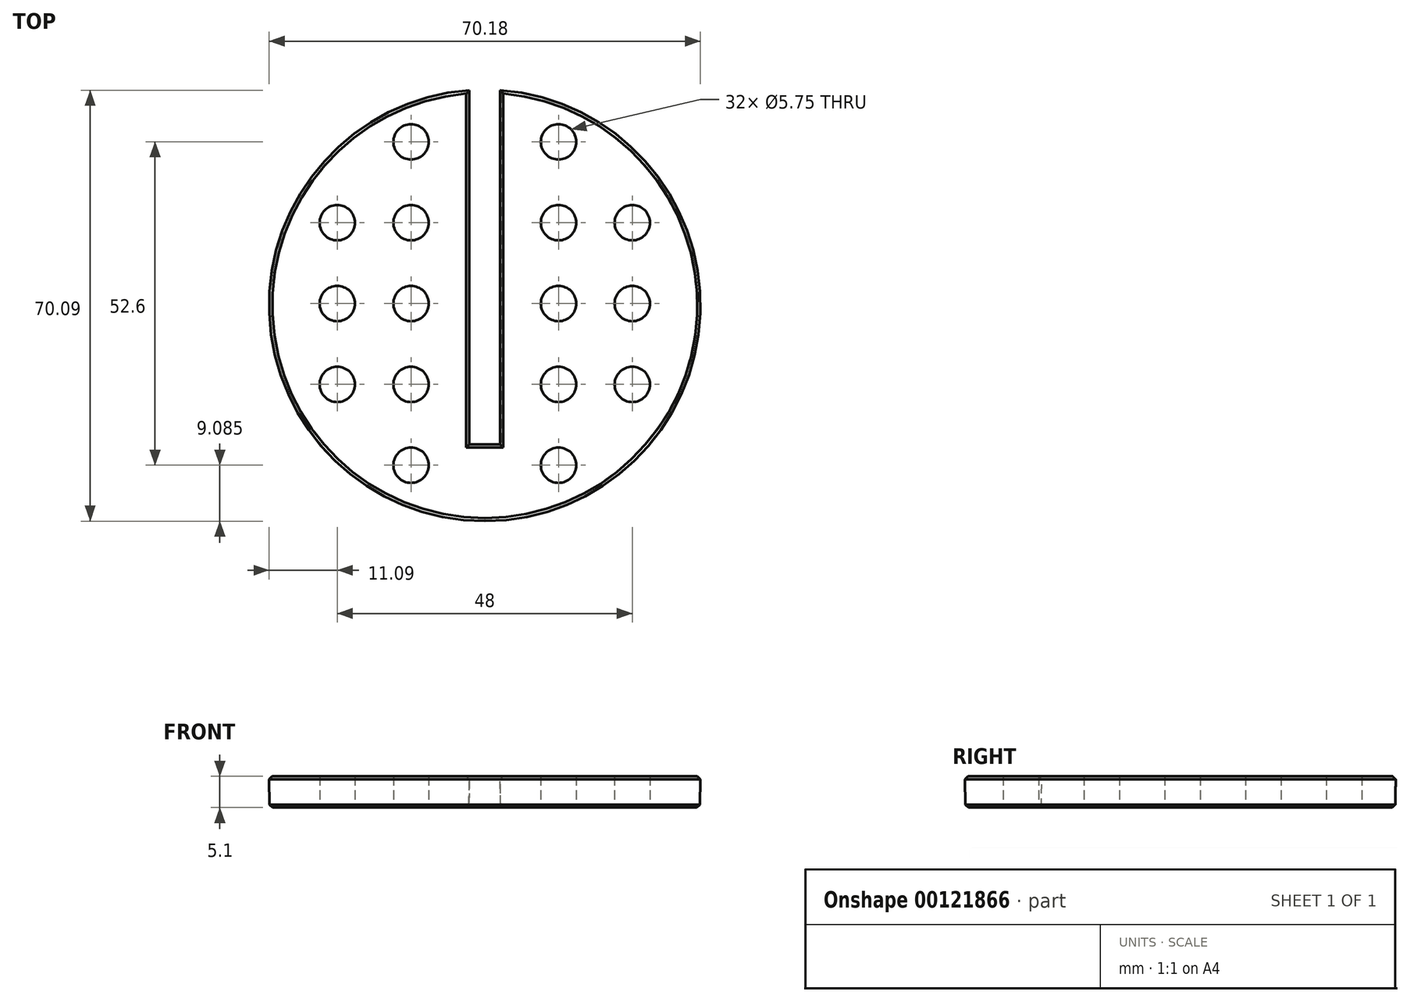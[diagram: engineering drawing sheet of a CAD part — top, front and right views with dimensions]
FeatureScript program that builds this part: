
annotation { "Feature Type Name" : "Feature", "Feature Type Description" : "" }
export const myFeature = defineFeature(function(context is Context, id is Id, definition is map)
    precondition{}
    {
        {
            var Q0;
            Q0=qCreatedBy(makeId("Top.planeOp"),FACE);
            var sketch = newSketch(context, id + "F0", { "sketchPlane" : qUnion([Q0])});
            skCircle(sketch, "E0", {"center": v(0, 0) * mm, "radius": 35.1 * mm});
            skPoint(sketch, "E1", {"position": v(-2.5, 0) * mm});
            skPoint(sketch, "E2", {"position": v(2.5, 0) * mm});
            skPoint(sketch, "E3", {"position": v(0, -35.1) * mm});
            skPoint(sketch, "E4", {"position": v(0, -22.6) * mm});
            skLineSegment(sketch, "E5", {"start": v(-2.5, 35) * mm, "end": v(-2.5, -22.6) * mm});
            skLineSegment(sketch, "E6", {"start": v(2.5, 35) * mm, "end": v(2.5, -22.6) * mm});
            skLineSegment(sketch, "E7", {"start": v(2.5, -22.6) * mm, "end": v(-2.5, -22.6) * mm});
            skPoint(sketch, "E8", {"position": v(-12, 26.6) * mm});
            skPoint(sketch, "E9.0.1.0", {"position": v(-12, 13.44) * mm});
            skPoint(sketch, "E9.0.2.0", {"position": v(-12, 0.3) * mm});
            skPoint(sketch, "E9.0.3.0", {"position": v(-12, -12.86) * mm});
            skPoint(sketch, "E9.0.4.0", {"position": v(-12, -26) * mm});
            skPoint(sketch, "E9.1.0.0", {"position": v(-24, 26.6) * mm});
            skPoint(sketch, "E9.1.1.0", {"position": v(-24, 13.44) * mm});
            skPoint(sketch, "E9.1.2.0", {"position": v(-24, 0.3) * mm});
            skPoint(sketch, "E9.1.3.0", {"position": v(-24, -12.86) * mm});
            skPoint(sketch, "E9.1.4.0", {"position": v(-24, -26) * mm});
            skLineSegment(sketch, "E9.direction1", {"start": v(-12, 26.6) * mm, "end": v(-24, 26.6) * mm, "construction": true});
            skLineSegment(sketch, "E9.direction2", {"start": v(-12, 26.6) * mm, "end": v(-12, 13.44) * mm, "construction": true});
            skPoint(sketch, "E10", {"position": v(0, 35.1) * mm});
            skLineSegment(sketch, "E11", {"start": v(0, 43.08) * mm, "end": v(0, -42.45) * mm, "construction": true});
            skPoint(sketch, "E12.MirrorP", {"position": v(24, -12.85) * mm});
            skPoint(sketch, "E13.MirrorP", {"position": v(24, 0.3) * mm});
            skPoint(sketch, "E14.MirrorP", {"position": v(24, 13.45) * mm});
            skPoint(sketch, "E15.MirrorP", {"position": v(12, -26) * mm});
            skPoint(sketch, "E16.MirrorP", {"position": v(12, -12.85) * mm});
            skPoint(sketch, "E17.MirrorP", {"position": v(12, 0.3) * mm});
            skPoint(sketch, "E18.MirrorP", {"position": v(12, 13.45) * mm});
            skPoint(sketch, "E19.MirrorP", {"position": v(12, 26.6) * mm});
            skSolve(sketch);
        }
        {
            var Q0;
            {var subQ0=sQuery(id+"F0.wireOp",EDGE,"E5");Q0=makeQuery(id+"F0.imprint","IMPRINT",FACE,{"disambiguationData":[TD([[makeQuery(id+"F0.imprint","IMPRINT",EDGE,{"derivedFrom":subQ0}),-1.0]])]});}
            extrude(context, id + "F1", {"entities" : qUnion([Q0]), "oppositeDirection" : true, "depth" : (4.72 + .381) * mm, "hasDraft" : true, "draftAngle" : 1 * degree, "draftPullDirection" : true});
        }
        {
            var Q0;
            Q0=sQuery(id+"F0.wireOp",VERTEX,"E8");
            var Q1;
            Q1=sQuery(id+"F0.wireOp",VERTEX,"E9.0.1.0");
            var Q2;
            Q2=sQuery(id+"F0.wireOp",VERTEX,"E9.0.2.0");
            var Q3;
            Q3=sQuery(id+"F0.wireOp",VERTEX,"E9.0.3.0");
            var Q4;
            Q4=sQuery(id+"F0.wireOp",VERTEX,"E9.1.2.0");
            var Q5;
            Q5=sQuery(id+"F0.wireOp",VERTEX,"E9.1.3.0");
            var Q6;
            Q6=sQuery(id+"F0.wireOp",VERTEX,"E9.1.1.0");
            var Q7;
            Q7=sQuery(id+"F0.wireOp",VERTEX,"E9.0.4.0");
            var Q8;
            Q8=sQuery(id+"F0.wireOp",VERTEX,"E14.MirrorP");
            var Q9;
            Q9=sQuery(id+"F0.wireOp",VERTEX,"E19.MirrorP");
            var Q10;
            Q10=sQuery(id+"F0.wireOp",VERTEX,"E15.MirrorP");
            var Q11;
            Q11=sQuery(id+"F0.wireOp",VERTEX,"E17.MirrorP");
            var Q12;
            Q12=sQuery(id+"F0.wireOp",VERTEX,"E12.MirrorP");
            var Q13;
            Q13=sQuery(id+"F0.wireOp",VERTEX,"E13.MirrorP");
            var Q14;
            Q14=sQuery(id+"F0.wireOp",VERTEX,"E18.MirrorP");
            var Q15;
            Q15=sQuery(id+"F0.wireOp",VERTEX,"E16.MirrorP");
            var Q16;
            Q16=makeQuery(id+"F1.opExtrude","SWEPT_BODY",BODY,{"disambiguationData":[OSD([sQuery(id+"F0.wireOp",EDGE,"E0"),sQuery(id+"F0.wireOp",EDGE,"E5"),sQuery(id+"F0.wireOp",EDGE,"E6"),sQuery(id+"F0.wireOp",EDGE,"E7")])]});
            hole(context, id + "F2", {"style" : HoleStyle.SIMPLE, "endStyle" : HoleEndStyle.BLIND, "holeDiameter" : 5.75 * mm, "holeDepth" : 7 * mm, "locations" : qUnion([Q0, Q1, Q2, Q3, Q4, Q5, Q6, Q7, Q8, Q9, Q10, Q11, Q12, Q13, Q14, Q15]), "scope" : qUnion([Q16])});
        }
        {
            var Q0;
            Q0=makeQuery(id+"F1.opExtrude","CAP_EDGE",EDGE,{"disambiguationData":[OSD([sQuery(id+"F0.wireOp",EDGE,"E0")])],"isStart":true});
            var Q1;
            Q1=makeQuery(id+"F1.opExtrude","CAP_EDGE",EDGE,{"disambiguationData":[OSD([sQuery(id+"F0.wireOp",EDGE,"E5")])],"isStart":true});
            var Q2;
            Q2=makeQuery(id+"F1.opExtrude","CAP_EDGE",EDGE,{"disambiguationData":[OSD([sQuery(id+"F0.wireOp",EDGE,"E7")])],"isStart":true});
            var Q3;
            Q3=makeQuery(id+"F1.opExtrude","CAP_EDGE",EDGE,{"disambiguationData":[OSD([sQuery(id+"F0.wireOp",EDGE,"E6")])],"isStart":true});
            var Q4;
            Q4=makeQuery(id+"F2.hole-0.boolean.opBoolean","COPY",EDGE,{"derivedFrom":makeQuery(id+"F2.hole-0.opRevolve","SWEPT_EDGE",EDGE,{"disambiguationData":[OSD([sQuery(id+"F2.hole-0.sketch.wireOp",EDGE,"core_line_2"),sQuery(id+"F2.hole-0.sketch.wireOp",EDGE,"core_line_3")])]})});
            var Q5;
            Q5=makeQuery(id+"F2.hole-1.boolean.opBoolean","COPY",EDGE,{"derivedFrom":makeQuery(id+"F2.hole-1.opRevolve","SWEPT_EDGE",EDGE,{"disambiguationData":[OSD([sQuery(id+"F2.hole-1.sketch.wireOp",EDGE,"core_line_2"),sQuery(id+"F2.hole-1.sketch.wireOp",EDGE,"core_line_3")])]})});
            var Q6;
            Q6=makeQuery(id+"F2.hole-2.boolean.opBoolean","COPY",EDGE,{"derivedFrom":makeQuery(id+"F2.hole-2.opRevolve","SWEPT_EDGE",EDGE,{"disambiguationData":[OSD([sQuery(id+"F2.hole-2.sketch.wireOp",EDGE,"core_line_2"),sQuery(id+"F2.hole-2.sketch.wireOp",EDGE,"core_line_3")])]})});
            var Q7;
            Q7=makeQuery(id+"F2.hole-3.boolean.opBoolean","COPY",EDGE,{"derivedFrom":makeQuery(id+"F2.hole-3.opRevolve","SWEPT_EDGE",EDGE,{"disambiguationData":[OSD([sQuery(id+"F2.hole-3.sketch.wireOp",EDGE,"core_line_2"),sQuery(id+"F2.hole-3.sketch.wireOp",EDGE,"core_line_3")])]})});
            var Q8;
            Q8=makeQuery(id+"F2.hole-7.boolean.opBoolean","COPY",EDGE,{"derivedFrom":makeQuery(id+"F2.hole-7.opRevolve","SWEPT_EDGE",EDGE,{"disambiguationData":[OSD([sQuery(id+"F2.hole-7.sketch.wireOp",EDGE,"core_line_2"),sQuery(id+"F2.hole-7.sketch.wireOp",EDGE,"core_line_3")])]})});
            var Q9;
            Q9=makeQuery(id+"F2.hole-5.boolean.opBoolean","COPY",EDGE,{"derivedFrom":makeQuery(id+"F2.hole-5.opRevolve","SWEPT_EDGE",EDGE,{"disambiguationData":[OSD([sQuery(id+"F2.hole-5.sketch.wireOp",EDGE,"core_line_2"),sQuery(id+"F2.hole-5.sketch.wireOp",EDGE,"core_line_3")])]})});
            var Q10;
            Q10=makeQuery(id+"F2.hole-4.boolean.opBoolean","COPY",EDGE,{"derivedFrom":makeQuery(id+"F2.hole-4.opRevolve","SWEPT_EDGE",EDGE,{"disambiguationData":[OSD([sQuery(id+"F2.hole-4.sketch.wireOp",EDGE,"core_line_2"),sQuery(id+"F2.hole-4.sketch.wireOp",EDGE,"core_line_3")])]})});
            var Q11;
            Q11=makeQuery(id+"F2.hole-6.boolean.opBoolean","COPY",EDGE,{"derivedFrom":makeQuery(id+"F2.hole-6.opRevolve","SWEPT_EDGE",EDGE,{"disambiguationData":[OSD([sQuery(id+"F2.hole-6.sketch.wireOp",EDGE,"core_line_2"),sQuery(id+"F2.hole-6.sketch.wireOp",EDGE,"core_line_3")])]})});
            var Q12;
            Q12=makeQuery(id+"F2.hole-11.boolean.opBoolean","COPY",EDGE,{"derivedFrom":makeQuery(id+"F2.hole-11.opRevolve","SWEPT_EDGE",EDGE,{"disambiguationData":[OSD([sQuery(id+"F2.hole-11.sketch.wireOp",EDGE,"core_line_2"),sQuery(id+"F2.hole-11.sketch.wireOp",EDGE,"core_line_3")])]})});
            var Q13;
            Q13=makeQuery(id+"F2.hole-14.boolean.opBoolean","COPY",EDGE,{"derivedFrom":makeQuery(id+"F2.hole-14.opRevolve","SWEPT_EDGE",EDGE,{"disambiguationData":[OSD([sQuery(id+"F2.hole-14.sketch.wireOp",EDGE,"core_line_2"),sQuery(id+"F2.hole-14.sketch.wireOp",EDGE,"core_line_3")])]})});
            var Q14;
            Q14=makeQuery(id+"F2.hole-9.boolean.opBoolean","COPY",EDGE,{"derivedFrom":makeQuery(id+"F2.hole-9.opRevolve","SWEPT_EDGE",EDGE,{"disambiguationData":[OSD([sQuery(id+"F2.hole-9.sketch.wireOp",EDGE,"core_line_2"),sQuery(id+"F2.hole-9.sketch.wireOp",EDGE,"core_line_3")])]})});
            var Q15;
            Q15=makeQuery(id+"F2.hole-8.boolean.opBoolean","COPY",EDGE,{"derivedFrom":makeQuery(id+"F2.hole-8.opRevolve","SWEPT_EDGE",EDGE,{"disambiguationData":[OSD([sQuery(id+"F2.hole-8.sketch.wireOp",EDGE,"core_line_2"),sQuery(id+"F2.hole-8.sketch.wireOp",EDGE,"core_line_3")])]})});
            var Q16;
            Q16=makeQuery(id+"F2.hole-13.boolean.opBoolean","COPY",EDGE,{"derivedFrom":makeQuery(id+"F2.hole-13.opRevolve","SWEPT_EDGE",EDGE,{"disambiguationData":[OSD([sQuery(id+"F2.hole-13.sketch.wireOp",EDGE,"core_line_2"),sQuery(id+"F2.hole-13.sketch.wireOp",EDGE,"core_line_3")])]})});
            var Q17;
            Q17=makeQuery(id+"F2.hole-12.boolean.opBoolean","COPY",EDGE,{"derivedFrom":makeQuery(id+"F2.hole-12.opRevolve","SWEPT_EDGE",EDGE,{"disambiguationData":[OSD([sQuery(id+"F2.hole-12.sketch.wireOp",EDGE,"core_line_2"),sQuery(id+"F2.hole-12.sketch.wireOp",EDGE,"core_line_3")])]})});
            var Q18;
            Q18=makeQuery(id+"F2.hole-15.boolean.opBoolean","COPY",EDGE,{"derivedFrom":makeQuery(id+"F2.hole-15.opRevolve","SWEPT_EDGE",EDGE,{"disambiguationData":[OSD([sQuery(id+"F2.hole-15.sketch.wireOp",EDGE,"core_line_2"),sQuery(id+"F2.hole-15.sketch.wireOp",EDGE,"core_line_3")])]})});
            var Q19;
            Q19=makeQuery(id+"F2.hole-10.boolean.opBoolean","COPY",EDGE,{"derivedFrom":makeQuery(id+"F2.hole-10.opRevolve","SWEPT_EDGE",EDGE,{"disambiguationData":[OSD([sQuery(id+"F2.hole-10.sketch.wireOp",EDGE,"core_line_2"),sQuery(id+"F2.hole-10.sketch.wireOp",EDGE,"core_line_3")])]})});
            var Q20;
            Q20=makeQuery(id+"F1.opExtrude","CAP_EDGE",EDGE,{"disambiguationData":[OSD([sQuery(id+"F0.wireOp",EDGE,"E0")])],"isStart":false});
            chamfer(context, id + "F3", {"entities" : qUnion([Q0, Q1, Q2, Q3, Q4, Q5, Q6, Q7, Q8, Q9, Q10, Q11, Q12, Q13, Q14, Q15, Q16, Q17, Q18, Q19, Q20]), "width" : .5 * mm, "tangentPropagation" : true});
        }
    });
